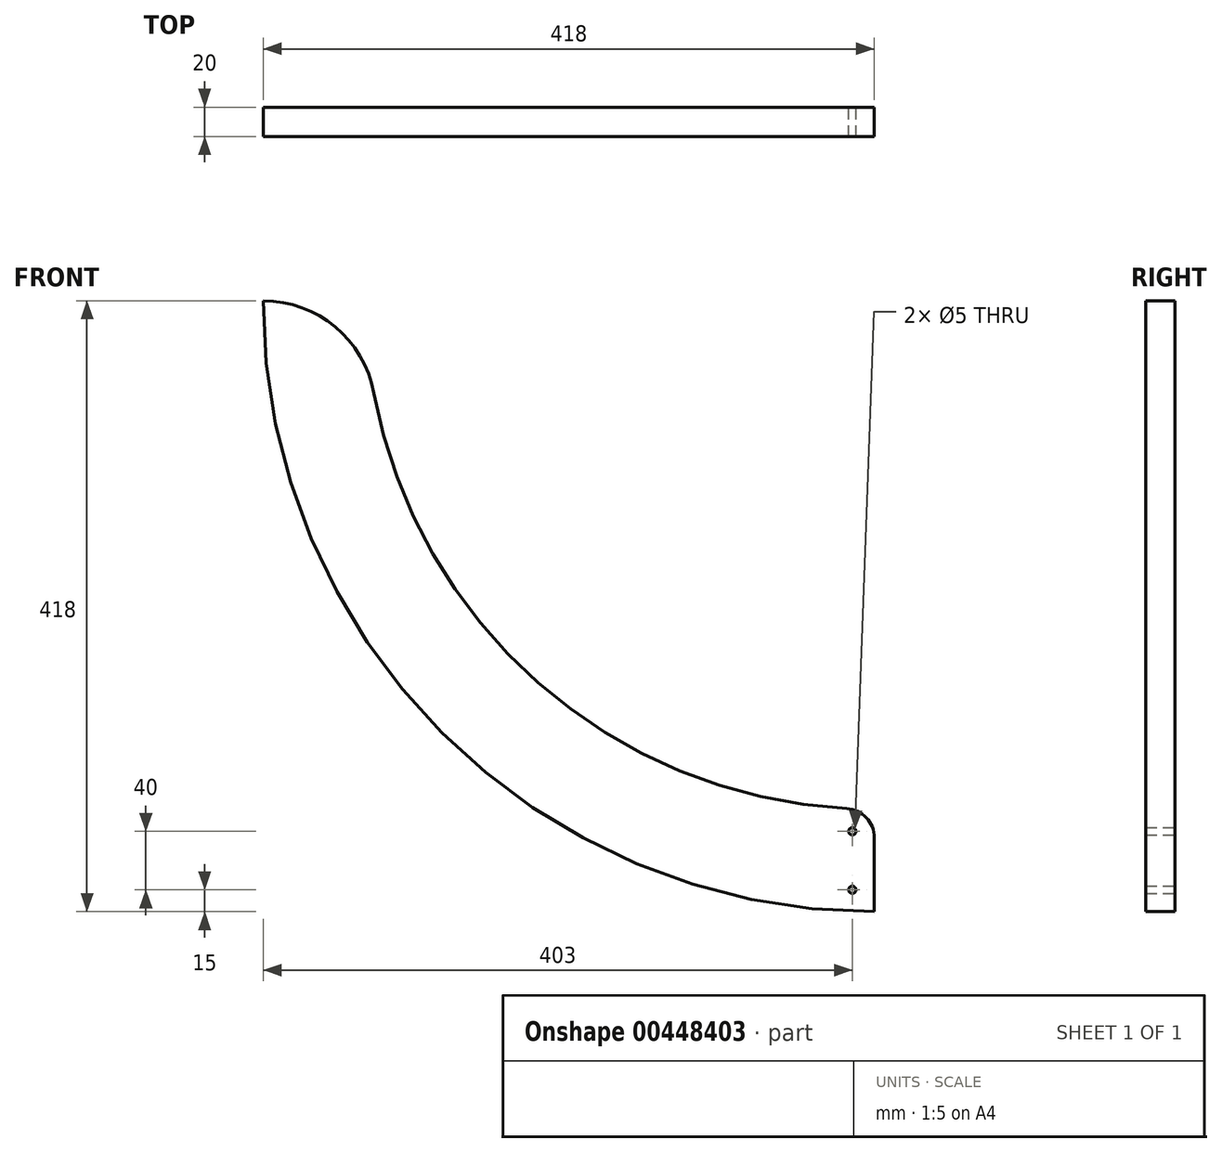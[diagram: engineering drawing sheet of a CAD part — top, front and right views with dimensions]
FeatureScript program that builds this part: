
annotation { "Feature Type Name" : "Feature", "Feature Type Description" : "" }
export const myFeature = defineFeature(function(context is Context, id is Id, definition is map)
    precondition{}
    {
        {
            var Q0;
            Q0=qCreatedBy(makeId("Front.planeOp"),FACE);
            var sketch = newSketch(context, id + "F0", { "sketchPlane" : qUnion([Q0])});
            skArc(sketch, "E0", {"start": v(-418, 418) * mm, "mid": v(-295.57, 122.43) * mm, "end": v(0, 0) * mm});
            skArc(sketch, "E1", {"start": v(-418, 418) * mm, "mid": v(-368.7, 400.17) * mm, "end": v(-342.24, 354.92) * mm});
            skLineSegment(sketch, "E2", {"start": v(-418, 418) * mm, "end": v(-418, 340.96) * mm, "construction": true});
            skArc(sketch, "E3", {"start": v(-342.24, 354.92) * mm, "mid": v(-229.85, 156.7) * mm, "end": v(-18.91, 70.51) * mm});
            skLineSegment(sketch, "E4", {"start": v(0, 0) * mm, "end": v(0, 50.54) * mm});
            skLineSegment(sketch, "E5.trimOffspring", {"start": v(0, 0) * mm, "end": v(0, 418) * mm, "construction": true});
            skArc(sketch, "E6", {"start": v(-18.91, 70.51) * mm, "mid": v(-5.48, 64.3) * mm, "end": v(0, 50.54) * mm});
            skLineSegment(sketch, "E7", {"start": v(0, 418) * mm, "end": v(-418, 418) * mm, "construction": true});
            skArc(sketch, "E8", {"start": v(-348, 418) * mm, "mid": v(-246.07, 171.93) * mm, "end": v(0, 70) * mm, "construction": true});
            skArc(sketch, "E9", {"start": v(-403, 418) * mm, "mid": v(-284.96, 133.04) * mm, "end": v(0, 15) * mm, "construction": true});
            skLineSegment(sketch, "E10", {"start": v(0, 418) * mm, "end": v(-22.72, 0.62) * mm, "construction": true});
            skCircle(sketch, "E11", {"center": v(-15, 55) * mm, "radius": 2.5 * mm});
            skLineSegment(sketch, "E12", {"start": v(-15, 0) * mm, "end": v(-15, 63.52) * mm, "construction": true});
            skLineSegment(sketch, "E13", {"start": v(0, 0) * mm, "end": v(-86.11, 0) * mm, "construction": true});
            skCircle(sketch, "E14", {"center": v(-15, 15) * mm, "radius": 2.5 * mm});
            skSolve(sketch);
        }
        {
            var Q0;
            Q0 = qSketchRegion(id + "F0", true);
            extrude(context, id + "F1", {"entities" : qUnion([Q0]), "depth" : 20 * mm});
        }
    });
